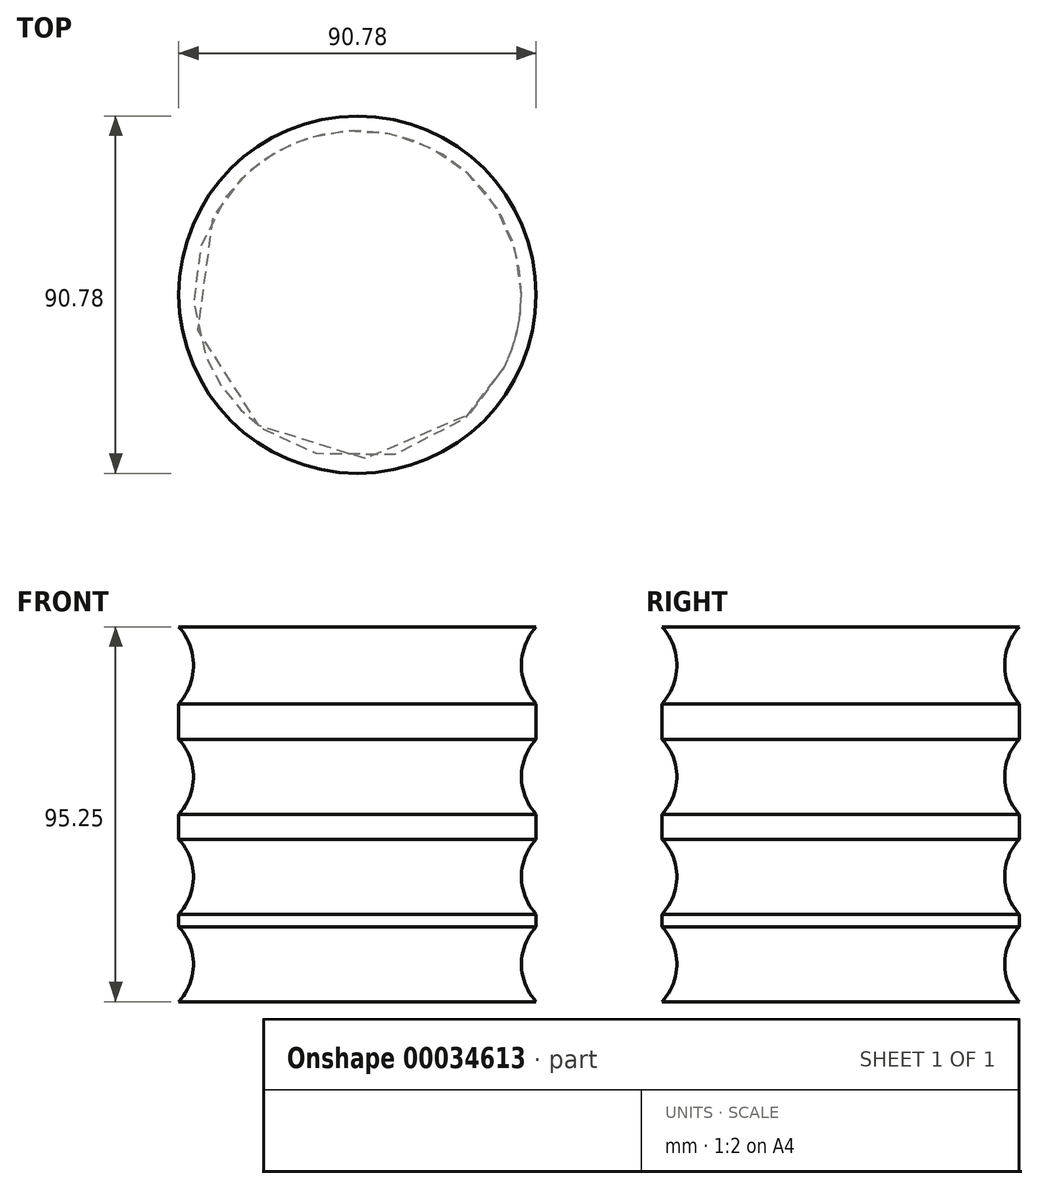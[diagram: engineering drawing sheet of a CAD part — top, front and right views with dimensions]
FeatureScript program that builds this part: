
annotation { "Feature Type Name" : "Feature", "Feature Type Description" : "" }
export const myFeature = defineFeature(function(context is Context, id is Id, definition is map)
    precondition{}
    {
        {
            var Q0;
            Q0=qCreatedBy(makeId("Front.planeOp"),FACE);
            var sketch = newSketch(context, id + "F0", { "sketchPlane" : qUnion([Q0])});
            skLineSegment(sketch, "E0", {"start": v(0, 53.66) * mm, "end": v(0, -72.35) * mm, "construction": true});
            skLineSegment(sketch, "E1.bottom", {"start": v(0, 53.66) * mm, "end": v(45.39, 53.66) * mm});
            skLineSegment(sketch, "E1.top", {"start": v(0, -41.59) * mm, "end": v(45.39, -41.59) * mm});
            skLineSegment(sketch, "E1.left", {"start": v(0, 53.66) * mm, "end": v(0, -41.59) * mm});
            skLineSegment(sketch, "E1.right", {"start": v(45.39, 53.66) * mm, "end": v(45.39, -41.59) * mm});
            skArc(sketch, "E2", {"start": v(45.39, 25.09) * mm, "mid": v(41.65, 15.56) * mm, "end": v(45.39, 6.04) * mm});
            skArc(sketch, "E3", {"start": v(45.39, -0.31) * mm, "mid": v(41.65, -9.84) * mm, "end": v(45.39, -19.36) * mm});
            skArc(sketch, "E4", {"start": v(45.39, -22.54) * mm, "mid": v(41.65, -32.06) * mm, "end": v(45.39, -41.59) * mm});
            skArc(sketch, "E5", {"start": v(45.39, 53.66) * mm, "mid": v(41.65, 43.88) * mm, "end": v(45.39, 34.1) * mm});
            skSolve(sketch);
        }
        {
            var Q0;
            Q0=makeQuery(id+"F0.imprint","IMPRINT",FACE,{"disambiguationData":[TD([[makeQuery(id+"F0.imprint","IMPRINT",EDGE,{"derivedFrom":sQuery(id+"F0.wireOp",EDGE,"E1.bottom")}),-1.0]])]});
            var Q1;
            Q1=sQuery(id+"F0.wireOp",EDGE,"E1.left");
            revolve(context, id + "F1", {"entities" : qUnion([Q0]), "axis" : qUnion([Q1]), "revolveType" : RevolveType.FULL});
        }
    });
